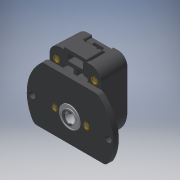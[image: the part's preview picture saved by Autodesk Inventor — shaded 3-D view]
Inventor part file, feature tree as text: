
AUTODESK INVENTOR PART (.ipt)
format: ipt  version: 2016 (Build 200138000, 138)  size: 2,918,400 bytes
history: native  units: mm
features: other x21, imported_body x20, extrude x1, sketch x1
ambient origin geometry x8: Origin, YZ Plane, XZ Plane, XY Plane, X Axis, Y Axis, Z Axis, Center Point
bodies: Body1 (feature_tree), Body2 (feature_tree), Body3 (feature_tree), Body4 (feature_tree), Body5 (feature_tree), Body6 (feature_tree), Body7 (feature_tree), Body8 (feature_tree), Body9 (feature_tree), Body10 (feature_tree), Body11 (feature_tree), Body12 (feature_tree), Body13 (feature_tree), Body14 (feature_tree), Body15 (feature_tree), Body16 (feature_tree), Body17 (feature_tree), Body18 (feature_tree), Body19 (feature_tree), Body20 (feature_tree)
feature tree (43):
  other  "3947.00-1_10509-1_10509-1-solid1"
  other  "H5-X-X-S1"
  extrude  "Extrusion1"  [1 undecoded]
  other  "3947.00-1_10509-1_10567-1-solid1"
  other  "3947.00-1_10509-1_10567-2-solid1"
  other  "3947.00-1_11428-3_11428-1-solid1"
  other  "3947.00-1_11428-3_10567-1-solid1"
  other  "3947.00-1_11428-3_10567-2-solid1"
  other  "3947.00-1_11428-3_10567-3-solid1"
  other  "3947.00-1_11428-3_10567-4-solid1"
  other  "3947.00-1_290-2-solid1"
  other  "3947.00-1_4-1-solid1"
  other  "3947.00-1_169-1-solid1"
  other  "3947.00-1_169-2-solid1"
  other  "3947.00-1_290-3-solid1"
  other  "11429-2-solid1"
  other  "10496-1-solid1"
  other  "4-1-solid1"
  other  "719-1-solid1"
  other  "719-2-solid1"
  other  "11934-1-solid1"
  other  "11934-2-solid1"
  imported_body  "Base1"
  imported_body  "Base2"
  imported_body  "Base3"
  imported_body  "Base4"
  imported_body  "Base5"
  imported_body  "Base6"
  imported_body  "Base7"
  imported_body  "Base8"
  imported_body  "Base9"
  imported_body  "Base10"
  imported_body  "Base12"
  imported_body  "Base13"
  imported_body  "Base14"
  imported_body  "Base15"
  imported_body  "Base16"
  imported_body  "Base17"
  imported_body  "Base18"
  imported_body  "Base19"
  imported_body  "Base20"
  imported_body  "Base21"
  sketch  "Sketch1"  dims[d0=3.81mm d1=0.0mm]
note: 1 required parameter value undecoded (feature->parameter linkage not recoverable at this tier; creation-order binding heuristic only, values carry confidence <= 0.55)
